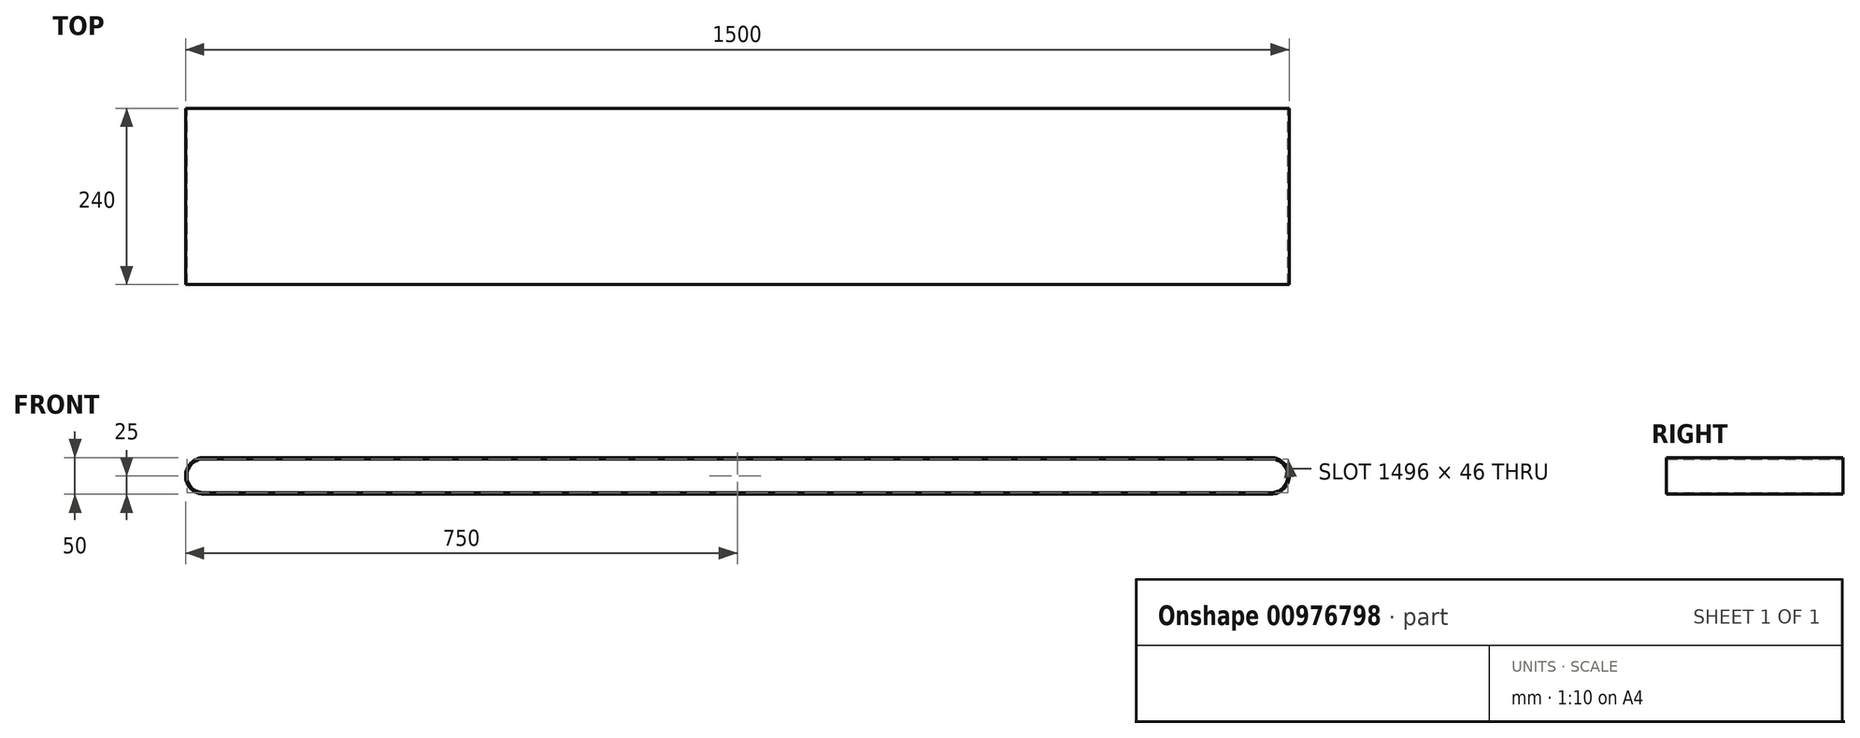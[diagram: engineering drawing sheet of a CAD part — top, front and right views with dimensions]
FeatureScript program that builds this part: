
annotation { "Feature Type Name" : "Feature", "Feature Type Description" : "" }
export const myFeature = defineFeature(function(context is Context, id is Id, definition is map)
    precondition{}
    {
        {
            var Q0;
            Q0=qCreatedBy(makeId("Front.planeOp"),FACE);
            var sketch = newSketch(context, id + "F0", { "sketchPlane" : qUnion([Q0])});
            skLineSegment(sketch, "E0", {"start": v(-898.42, 0) * mm, "end": v(825.08, 0) * mm, "construction": true});
            skLineSegment(sketch, "E1", {"start": v(0, 588.08) * mm, "end": v(0, -575.6) * mm, "construction": true});
            skArc(sketch, "E2", {"start": v(725, -25) * mm, "mid": v(750, 0) * mm, "end": v(725, 25) * mm});
            skArc(sketch, "E3", {"start": v(-725, 25) * mm, "mid": v(-750, 0) * mm, "end": v(-725, -25) * mm});
            skLineSegment(sketch, "E4", {"start": v(-725, 25) * mm, "end": v(725, 25) * mm});
            skLineSegment(sketch, "E5", {"start": v(-725, -25) * mm, "end": v(725, -25) * mm});
            skLineSegment(sketch, "E6.0", {"start": v(-725, 23) * mm, "end": v(725, 23) * mm});
            skArc(sketch, "E6.1", {"start": v(-725, 23) * mm, "mid": v(-748, 0) * mm, "end": v(-725, -23) * mm});
            skLineSegment(sketch, "E6.2", {"start": v(-725, -23) * mm, "end": v(725, -23) * mm});
            skArc(sketch, "E6.3", {"start": v(725, -23) * mm, "mid": v(748, 0) * mm, "end": v(725, 23) * mm});
            skSolve(sketch);
        }
        {
            var Q0;
            Q0=makeQuery(id+"F0.imprint","IMPRINT",FACE,{"disambiguationData":[TD([[makeQuery(id+"F0.imprint","IMPRINT",EDGE,{"derivedFrom":sQuery(id+"F0.wireOp",EDGE,"E2")}),1.0]])]});
            extrude(context, id + "F1", {"entities" : qUnion([Q0]), "endBound" : BoundingType.SYMMETRIC, "depth" : 240 * mm, "offsetDistance" : 25.4 * mm});
        }
    });
